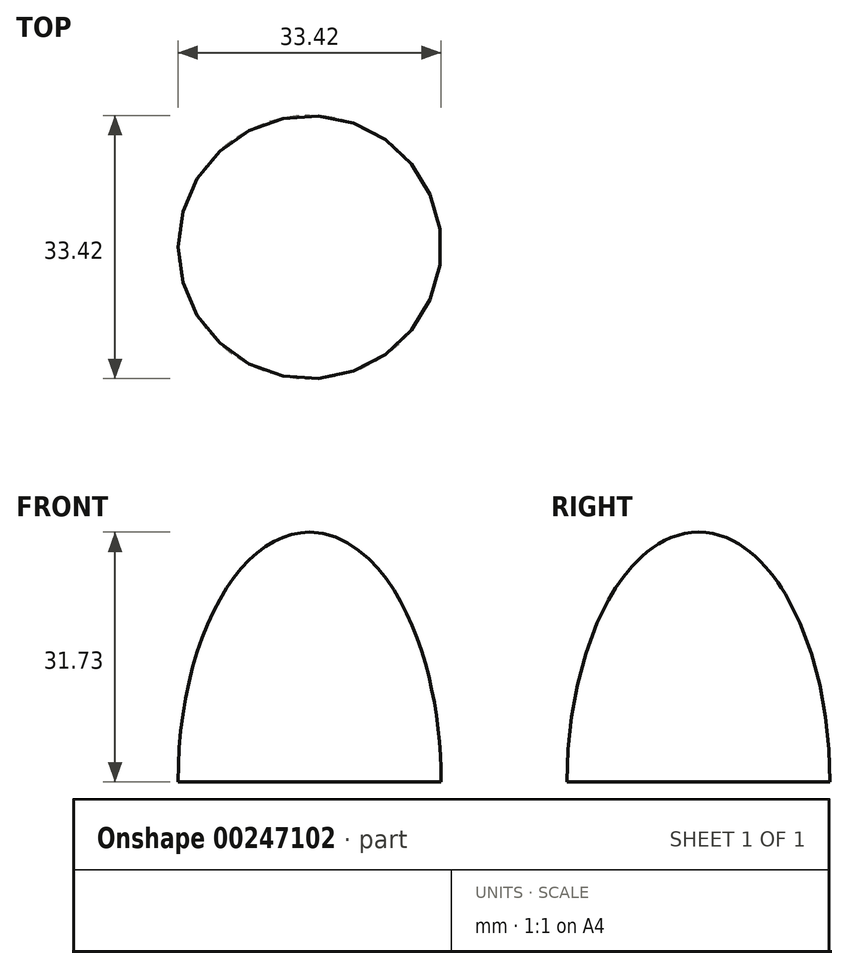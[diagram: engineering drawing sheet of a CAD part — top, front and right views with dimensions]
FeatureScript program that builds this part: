
annotation { "Feature Type Name" : "Feature", "Feature Type Description" : "" }
export const myFeature = defineFeature(function(context is Context, id is Id, definition is map)
    precondition{}
    {
        {
            var Q0;
            Q0=qCreatedBy(makeId("Front.planeOp"),FACE);
            var sketch = newSketch(context, id + "F0", { "sketchPlane" : qUnion([Q0])});
            skEllipticalArc(sketch, "E0", {});
            skLineSegment(sketch, "E1", {"start": v(-16.7, 0) * mm, "end": v(0, 0) * mm});
            skLineSegment(sketch, "E2", {"start": v(0, 0) * mm, "end": v(0, 31.73) * mm});
            skPoint(sketch, "E3.orphan", {"position": v(16.7, 0) * mm});
            const initialGuessF0  = {"E0": [0, 0, 0, 1, 0.03173072263598442, 0.01670975628647444, 0, 1.5707963267948966]};
            skSetInitialGuess(sketch, initialGuessF0);
            skSolve(sketch);
        }
        {
            var Q0;
            Q0=makeQuery(id+"F0.imprint","IMPRINT",FACE,{"disambiguationData":[TD([[makeQuery(id+"F0.imprint","IMPRINT",EDGE,{"derivedFrom":sQuery(id+"F0.wireOp",EDGE,"E0")}),1.0]])]});
            var Q1;
            Q1=sQuery(id+"F0.wireOp",EDGE,"E2");
            revolve(context, id + "F1", {"entities" : qUnion([Q0]), "axis" : qUnion([Q1]), "revolveType" : RevolveType.FULL});
        }
    });
